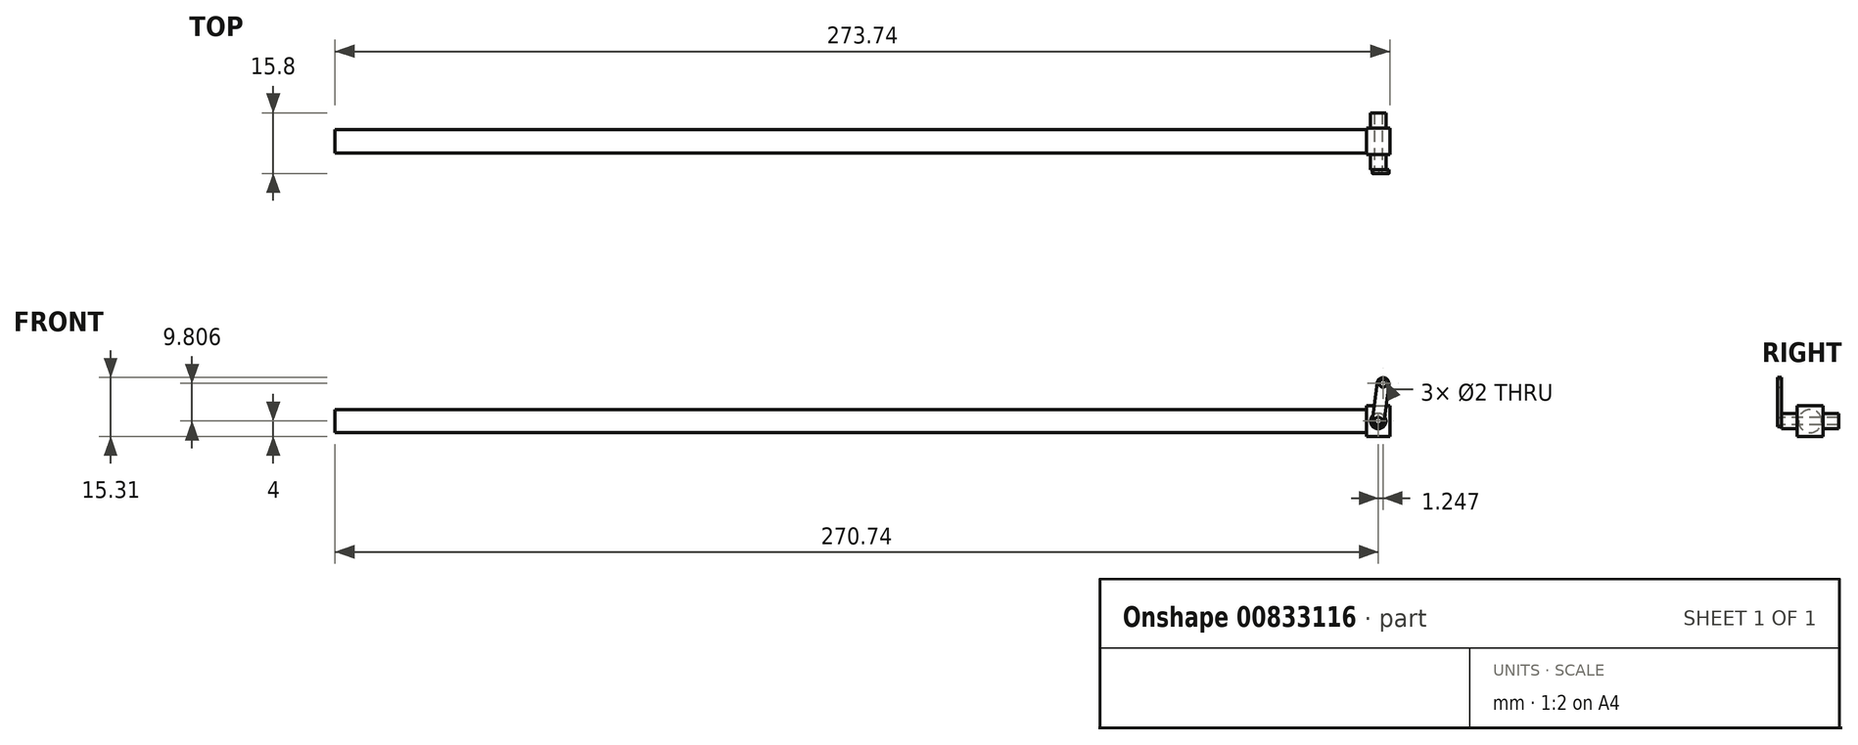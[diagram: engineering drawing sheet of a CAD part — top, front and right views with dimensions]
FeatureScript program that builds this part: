
annotation { "Feature Type Name" : "Feature", "Feature Type Description" : "" }
export const myFeature = defineFeature(function(context is Context, id is Id, definition is map)
    precondition{}
    {
        {
            var Q0;
            Q0=qCreatedBy(makeId("Front.planeOp"),FACE);
            var sketch = newSketch(context, id + "F0", { "sketchPlane" : qUnion([Q0])});
            skLineSegment(sketch, "E0.bottom", {"start": v(-3, 4) * mm, "end": v(3, 4) * mm});
            skLineSegment(sketch, "E0.top", {"start": v(-3, -4) * mm, "end": v(3, -4) * mm});
            skLineSegment(sketch, "E0.left", {"start": v(-3, 4) * mm, "end": v(-3, -4) * mm});
            skLineSegment(sketch, "E0.right", {"start": v(3, 4) * mm, "end": v(3, -4) * mm});
            skPoint(sketch, "E0.middle", {"position": v(0, 0) * mm});
            skSolve(sketch);
        }
        {
            var Q0;
            Q0=makeQuery(id+"F0.imprint","IMPRINT",FACE,{"disambiguationData":[TD([[makeQuery(id+"F0.imprint","IMPRINT",EDGE,{"derivedFrom":sQuery(id+"F0.wireOp",EDGE,"E0.bottom")}),-1.0]])]});
            extrude(context, id + "F1", {"entities" : qUnion([Q0]), "endBound" : BoundingType.SYMMETRIC, "depth" : (6.8 + 8) * mm, "offsetDistance" : 25 * mm});
        }
        {
            var Q0;
            Q0=makeQuery(id+"F1.opExtrude","CAP_FACE",FACE,{"disambiguationData":[OSD([sQuery(id+"F0.wireOp",EDGE,"E0.bottom"),sQuery(id+"F0.wireOp",EDGE,"E0.top"),sQuery(id+"F0.wireOp",EDGE,"E0.left"),sQuery(id+"F0.wireOp",EDGE,"E0.right")])],"isStart":false});
            var sketch = newSketch(context, id + "F2", { "sketchPlane" : qUnion([Q0])});
            skCircle(sketch, "E1", {"center": v(0, 0) * mm, "radius": 2 * mm});
            skSolve(sketch);
        }
        {
            var Q0;
            Q0=makeQuery(id+"F2.imprint","IMPRINT",FACE,{"disambiguationData":[TD([[makeQuery(id+"F2.imprint","IMPRINT",EDGE,{"derivedFrom":sQuery(id+"F2.wireOp",EDGE,"E1")}),-1.0]])]});
            extrude(context, id + "F3", {"entities" : qUnion([Q0]), "operationType" : NewBodyOperationType.REMOVE, "oppositeDirection" : true, "depth" : 4 * mm, "offsetDistance" : 25 * mm});
        }
        {
            var Q0;
            Q0=makeQuery(id+"F1.opExtrude","CAP_FACE",FACE,{"disambiguationData":[OSD([sQuery(id+"F0.wireOp",EDGE,"E0.bottom"),sQuery(id+"F0.wireOp",EDGE,"E0.top"),sQuery(id+"F0.wireOp",EDGE,"E0.left"),sQuery(id+"F0.wireOp",EDGE,"E0.right")])],"isStart":true});
            var sketch = newSketch(context, id + "F4", { "sketchPlane" : qUnion([Q0])});
            skCircle(sketch, "E2", {"center": v(0, 0) * mm, "radius": 2 * mm});
            skSolve(sketch);
        }
        {
            var Q0;
            Q0=makeQuery(id+"F4.imprint","IMPRINT",FACE,{"disambiguationData":[TD([[makeQuery(id+"F4.imprint","IMPRINT",EDGE,{"derivedFrom":sQuery(id+"F4.wireOp",EDGE,"E2")}),-1.0]])]});
            extrude(context, id + "F5", {"entities" : qUnion([Q0]), "operationType" : NewBodyOperationType.REMOVE, "oppositeDirection" : true, "depth" : 4 * mm, "offsetDistance" : 25 * mm});
        }
        {
            var Q0;
            Q0=makeQuery(id+"F1.opExtrude","SWEPT_FACE",FACE,{"disambiguationData":[OSD([sQuery(id+"F0.wireOp",EDGE,"E0.left")])]});
            var sketch = newSketch(context, id + "F6", { "sketchPlane" : qUnion([Q0])});
            skCircle(sketch, "E3", {"center": v(0, 0) * mm, "radius": 3 * mm});
            skSolve(sketch);
        }
        {
            var Q0;
            Q0=makeQuery(id+"F6.imprint","IMPRINT",FACE,{"disambiguationData":[TD([[makeQuery(id+"F6.imprint","IMPRINT",EDGE,{"derivedFrom":sQuery(id+"F6.wireOp",EDGE,"E3")}),1.0]])]});
            extrude(context, id + "F7", {"entities" : qUnion([Q0]), "operationType" : NewBodyOperationType.ADD, "depth" : (170.74 - 3) * mm, "offsetDistance" : 25 * mm});
        }
        {
            var Q0;
            Q0=makeQuery(id+"F7.opExtrude","CAP_FACE",FACE,{"disambiguationData":[OSD([sQuery(id+"F6.wireOp",EDGE,"E3")])],"isStart":false});
            var sketch = newSketch(context, id + "F8", { "sketchPlane" : qUnion([Q0])});
            skCircle(sketch, "E4", {"center": v(0, 0) * mm, "radius": 3 * mm});
            skSolve(sketch);
        }
        {
            var Q0;
            Q0=makeQuery(id+"F8.imprint","IMPRINT",FACE,{"disambiguationData":[TD([[makeQuery(id+"F8.imprint","IMPRINT",EDGE,{"derivedFrom":sQuery(id+"F8.wireOp",EDGE,"E4")}),1.0]])]});
            extrude(context, id + "F9", {"entities" : qUnion([Q0]), "operationType" : NewBodyOperationType.ADD, "depth" : 100 * mm, "offsetDistance" : 25 * mm});
        }
        {
            var Q0;
            Q0=makeQuery(id+"F1.opExtrude","CAP_FACE",FACE,{"disambiguationData":[OSD([sQuery(id+"F0.wireOp",EDGE,"E0.bottom"),sQuery(id+"F0.wireOp",EDGE,"E0.top"),sQuery(id+"F0.wireOp",EDGE,"E0.left"),sQuery(id+"F0.wireOp",EDGE,"E0.right")])],"isStart":false});
            var sketch = newSketch(context, id + "F10", { "sketchPlane" : qUnion([Q0])});
            skCircle(sketch, "E5", {"center": v(0, 0) * mm, "radius": 1 * mm});
            skLineSegment(sketch, "E6", {"start": v(0, 2) * mm, "end": v(0, -2) * mm, "construction": true});
            skLineSegment(sketch, "E7", {"start": v(-2.88, 16.67) * mm, "end": v(-2.96, 16.68) * mm});
            skLineSegment(sketch, "E8", {"start": v(-2.88, 16.67) * mm, "end": v(6.96, 15.44) * mm, "construction": true});
            skLineSegment(sketch, "E9.trimOffspring", {"start": v(1.25, 9.8) * mm, "end": v(0, 0) * mm});
            skCircle(sketch, "E10", {"center": v(1.25, 9.8) * mm, "radius": 1 * mm});
            skArc(sketch, "E11.0.startCap", {"start": v(-0.24, 10) * mm, "mid": v(1.44, 11.3) * mm, "end": v(2.73, 9.62) * mm});
            skArc(sketch, "E11.0.endCap", {"start": v(1.49, -0.19) * mm, "mid": v(-0.19, -1.49) * mm, "end": v(-1.49, 0.19) * mm});
            skLineSegment(sketch, "E11.0.left", {"start": v(2.73, 9.62) * mm, "end": v(1.49, -0.19) * mm});
            skLineSegment(sketch, "E11.0.right", {"start": v(-0.24, 10) * mm, "end": v(-1.49, 0.19) * mm});
            skPoint(sketch, "E12.orphan", {"position": v(2.04, 16.06) * mm});
            skLineSegment(sketch, "E13", {"start": v(0, 0) * mm, "end": v(2.04, 16.06) * mm, "construction": true});
            skLineSegment(sketch, "E14", {"start": v(0, 0) * mm, "end": v(-8.48, 0) * mm, "construction": true});
            skSolve(sketch);
        }
        {
            var Q0;
            Q0=makeQuery(id+"F10.imprint","IMPRINT",FACE,{"disambiguationData":[TD([[makeQuery(id+"F10.imprint","IMPRINT",EDGE,{"derivedFrom":sQuery(id+"F10.wireOp",EDGE,"E5")}),1.0]])]});
            extrude(context, id + "F11", {"entities" : qUnion([Q0]), "operationType" : NewBodyOperationType.REMOVE, "endBound" : BoundingType.THROUGH_ALL, "oppositeDirection" : true, "depth" : 25 * mm, "offsetDistance" : 25 * mm});
        }
        {
            var Q0;
            Q0=makeQuery(id+"F10.imprint","IMPRINT",FACE,{"disambiguationData":[TD([[makeQuery(id+"F10.imprint","IMPRINT",EDGE,{"derivedFrom":sQuery(id+"F10.wireOp",EDGE,"E10")}),-1.0]])]});
            var Q1;
            Q1=makeQuery(id+"F10.imprint","IMPRINT",FACE,{"disambiguationData":[TD([[makeQuery(id+"F10.imprint","IMPRINT",EDGE,{"derivedFrom":sQuery(id+"F10.wireOp",EDGE,"E5")}),-1.0]])]});
            extrude(context, id + "F12", {"entities" : qUnion([Q0, Q1]), "depth" : 1 * mm, "offsetDistance" : 25 * mm});
        }
    });
